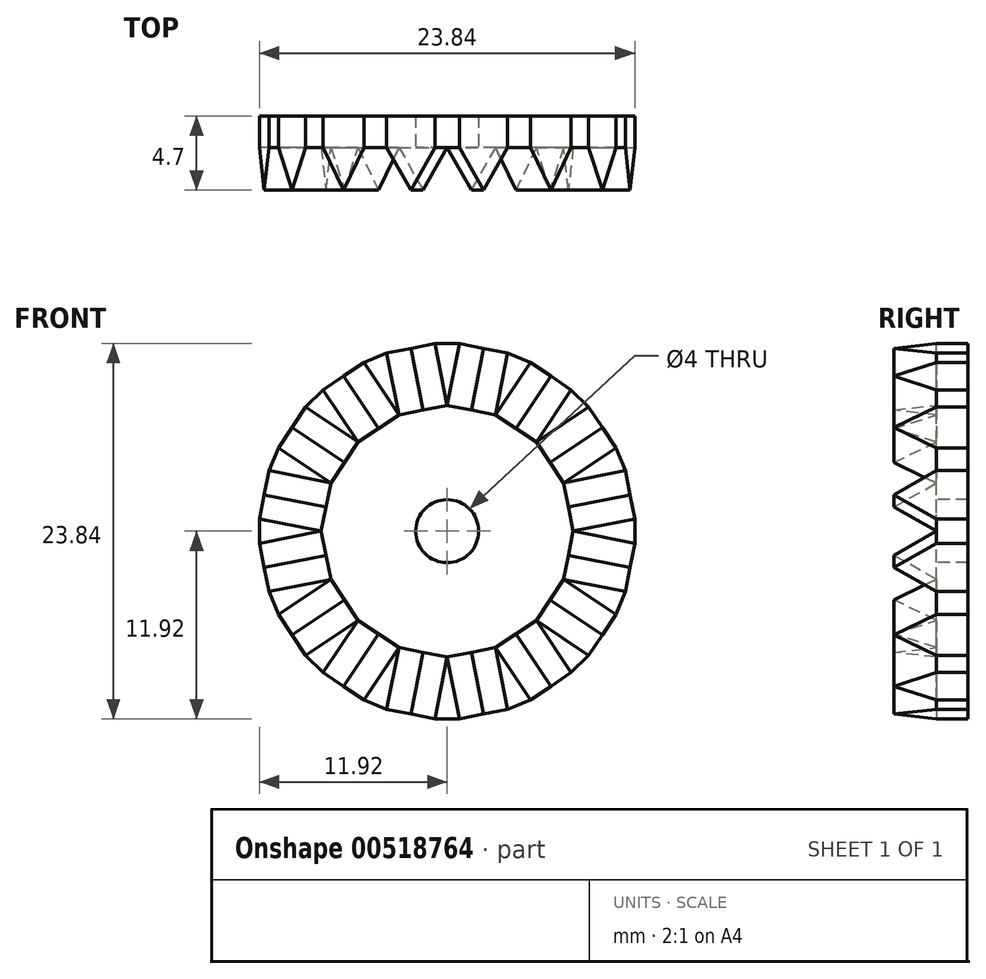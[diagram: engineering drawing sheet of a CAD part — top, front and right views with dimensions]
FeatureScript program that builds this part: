
annotation { "Feature Type Name" : "Feature", "Feature Type Description" : "" }
export const myFeature = defineFeature(function(context is Context, id is Id, definition is map)
    precondition{}
    {
        {
            var Q0;
            Q0=qCreatedBy(makeId("Front.planeOp"),FACE);
            var sketch = newSketch(context, id + "F0", { "sketchPlane" : qUnion([Q0])});
            skCircle(sketch, "E0", {"center": v(0, 0) * mm, "radius": 8 * mm, "construction": true});
            skCircle(sketch, "E1", {"center": v(0, 0) * mm, "radius": 2 * mm});
            skLineSegment(sketch, "E2", {"start": v(0, 0) * mm, "end": v(-3.06, 7.4) * mm, "construction": true});
            skLineSegment(sketch, "E3", {"start": v(-3.06, 7.4) * mm, "end": v(0, 8) * mm});
            skLineSegment(sketch, "E4.1.0", {"start": v(-5.66, 5.66) * mm, "end": v(-3.06, 7.4) * mm});
            skLineSegment(sketch, "E4.2.0", {"start": v(-7.4, 3.06) * mm, "end": v(-5.66, 5.66) * mm});
            skLineSegment(sketch, "E4.3.0", {"start": v(-8, 0) * mm, "end": v(-7.4, 3.06) * mm});
            skLineSegment(sketch, "E4.4.0", {"start": v(-7.4, -3.06) * mm, "end": v(-8, 0) * mm});
            skLineSegment(sketch, "E4.5.0", {"start": v(-5.66, -5.66) * mm, "end": v(-7.4, -3.06) * mm});
            skLineSegment(sketch, "E4.6.0", {"start": v(-3.06, -7.4) * mm, "end": v(-5.66, -5.66) * mm});
            skLineSegment(sketch, "E4.7.0", {"start": v(0, -8) * mm, "end": v(-3.06, -7.4) * mm});
            skLineSegment(sketch, "E4.8.0", {"start": v(3.06, -7.4) * mm, "end": v(0, -8) * mm});
            skLineSegment(sketch, "E4.9.0", {"start": v(5.66, -5.66) * mm, "end": v(3.06, -7.4) * mm});
            skLineSegment(sketch, "E4.10.0", {"start": v(7.4, -3.06) * mm, "end": v(5.66, -5.66) * mm});
            skLineSegment(sketch, "E4.11.0", {"start": v(8, 0) * mm, "end": v(7.4, -3.06) * mm});
            skLineSegment(sketch, "E4.12.0", {"start": v(7.4, 3.06) * mm, "end": v(8, 0) * mm});
            skLineSegment(sketch, "E4.13.0", {"start": v(5.66, 5.66) * mm, "end": v(7.4, 3.06) * mm});
            skLineSegment(sketch, "E4.14.0", {"start": v(3.06, 7.4) * mm, "end": v(5.66, 5.66) * mm});
            skLineSegment(sketch, "E4.15.0", {"start": v(0, 8) * mm, "end": v(3.06, 7.4) * mm});
            skLineSegment(sketch, "E5", {"start": v(-3.06, 7.4) * mm, "end": v(-5.28, 10.72) * mm});
            skLineSegment(sketch, "E6", {"start": v(-5.28, 10.72) * mm, "end": v(-3.84, 11.31) * mm});
            skLineSegment(sketch, "E7", {"start": v(-3.84, 11.31) * mm, "end": v(-3.06, 7.4) * mm});
            skLineSegment(sketch, "E8.1.0", {"start": v(-8.98, 7.88) * mm, "end": v(-7.88, 8.98) * mm});
            skLineSegment(sketch, "E8.1.1", {"start": v(-5.66, 5.66) * mm, "end": v(-8.98, 7.88) * mm});
            skLineSegment(sketch, "E8.1.2", {"start": v(-7.88, 8.98) * mm, "end": v(-5.66, 5.66) * mm});
            skLineSegment(sketch, "E8.2.0", {"start": v(-11.31, 3.84) * mm, "end": v(-10.72, 5.28) * mm});
            skLineSegment(sketch, "E8.2.1", {"start": v(-7.4, 3.06) * mm, "end": v(-11.31, 3.84) * mm});
            skLineSegment(sketch, "E8.2.2", {"start": v(-10.72, 5.28) * mm, "end": v(-7.4, 3.06) * mm});
            skLineSegment(sketch, "E8.3.0", {"start": v(-11.92, -0.78) * mm, "end": v(-11.92, 0.78) * mm});
            skLineSegment(sketch, "E8.3.1", {"start": v(-8, 0) * mm, "end": v(-11.92, -0.78) * mm});
            skLineSegment(sketch, "E8.3.2", {"start": v(-11.92, 0.78) * mm, "end": v(-8, 0) * mm});
            skLineSegment(sketch, "E8.4.0", {"start": v(-10.72, -5.28) * mm, "end": v(-11.31, -3.84) * mm});
            skLineSegment(sketch, "E8.4.1", {"start": v(-7.4, -3.06) * mm, "end": v(-10.72, -5.28) * mm});
            skLineSegment(sketch, "E8.4.2", {"start": v(-11.31, -3.84) * mm, "end": v(-7.4, -3.06) * mm});
            skLineSegment(sketch, "E8.5.0", {"start": v(-7.88, -8.98) * mm, "end": v(-8.98, -7.88) * mm});
            skLineSegment(sketch, "E8.5.1", {"start": v(-5.66, -5.66) * mm, "end": v(-7.88, -8.98) * mm});
            skLineSegment(sketch, "E8.5.2", {"start": v(-8.98, -7.88) * mm, "end": v(-5.66, -5.66) * mm});
            skLineSegment(sketch, "E8.6.0", {"start": v(-3.84, -11.31) * mm, "end": v(-5.28, -10.72) * mm});
            skLineSegment(sketch, "E8.6.1", {"start": v(-3.06, -7.4) * mm, "end": v(-3.84, -11.31) * mm});
            skLineSegment(sketch, "E8.6.2", {"start": v(-5.28, -10.72) * mm, "end": v(-3.06, -7.4) * mm});
            skLineSegment(sketch, "E8.7.0", {"start": v(0.78, -11.92) * mm, "end": v(-0.78, -11.92) * mm});
            skLineSegment(sketch, "E8.7.1", {"start": v(0, -8) * mm, "end": v(0.78, -11.92) * mm});
            skLineSegment(sketch, "E8.7.2", {"start": v(-0.78, -11.92) * mm, "end": v(0, -8) * mm});
            skLineSegment(sketch, "E8.8.0", {"start": v(5.28, -10.72) * mm, "end": v(3.84, -11.31) * mm});
            skLineSegment(sketch, "E8.8.1", {"start": v(3.06, -7.4) * mm, "end": v(5.28, -10.72) * mm});
            skLineSegment(sketch, "E8.8.2", {"start": v(3.84, -11.31) * mm, "end": v(3.06, -7.4) * mm});
            skLineSegment(sketch, "E8.9.0", {"start": v(8.98, -7.88) * mm, "end": v(7.88, -8.98) * mm});
            skLineSegment(sketch, "E8.9.1", {"start": v(5.66, -5.66) * mm, "end": v(8.98, -7.88) * mm});
            skLineSegment(sketch, "E8.9.2", {"start": v(7.88, -8.98) * mm, "end": v(5.66, -5.66) * mm});
            skLineSegment(sketch, "E8.10.0", {"start": v(11.31, -3.84) * mm, "end": v(10.72, -5.28) * mm});
            skLineSegment(sketch, "E8.10.1", {"start": v(7.4, -3.06) * mm, "end": v(11.31, -3.84) * mm});
            skLineSegment(sketch, "E8.10.2", {"start": v(10.72, -5.28) * mm, "end": v(7.4, -3.06) * mm});
            skLineSegment(sketch, "E8.11.0", {"start": v(11.92, 0.78) * mm, "end": v(11.92, -0.78) * mm});
            skLineSegment(sketch, "E8.11.1", {"start": v(8, 0) * mm, "end": v(11.92, 0.78) * mm});
            skLineSegment(sketch, "E8.11.2", {"start": v(11.92, -0.78) * mm, "end": v(8, 0) * mm});
            skLineSegment(sketch, "E8.12.0", {"start": v(10.72, 5.28) * mm, "end": v(11.31, 3.84) * mm});
            skLineSegment(sketch, "E8.12.1", {"start": v(7.4, 3.06) * mm, "end": v(10.72, 5.28) * mm});
            skLineSegment(sketch, "E8.12.2", {"start": v(11.31, 3.84) * mm, "end": v(7.4, 3.06) * mm});
            skLineSegment(sketch, "E8.13.0", {"start": v(7.88, 8.98) * mm, "end": v(8.98, 7.88) * mm});
            skLineSegment(sketch, "E8.13.1", {"start": v(5.66, 5.66) * mm, "end": v(7.88, 8.98) * mm});
            skLineSegment(sketch, "E8.13.2", {"start": v(8.98, 7.88) * mm, "end": v(5.66, 5.66) * mm});
            skLineSegment(sketch, "E8.14.0", {"start": v(3.84, 11.31) * mm, "end": v(5.28, 10.72) * mm});
            skLineSegment(sketch, "E8.14.1", {"start": v(3.06, 7.4) * mm, "end": v(3.84, 11.31) * mm});
            skLineSegment(sketch, "E8.14.2", {"start": v(5.28, 10.72) * mm, "end": v(3.06, 7.4) * mm});
            skLineSegment(sketch, "E8.15.0", {"start": v(-0.78, 11.92) * mm, "end": v(0.78, 11.92) * mm});
            skLineSegment(sketch, "E8.15.1", {"start": v(0, 8) * mm, "end": v(-0.78, 11.92) * mm});
            skLineSegment(sketch, "E8.15.2", {"start": v(0.78, 11.92) * mm, "end": v(0, 8) * mm});
            skSolve(sketch);
        }
        {
            var Q0;
            Q0 = qSketchRegion(id + "F0", true);
            extrude(context, id + "F1", {"entities" : qUnion([Q0]), "oppositeDirection" : true, "depth" : 2 * mm, "offsetDistance" : 25 * mm});
        }
        {
            var Q0;
            Q0=makeQuery(id+"F1.opExtrude","SWEPT_FACE",FACE,{"disambiguationData":[OSD([sQuery(id+"F0.wireOp",EDGE,"E3")])]});
            var sketch = newSketch(context, id + "F2", { "sketchPlane" : qUnion([Q0])});
            skLineSegment(sketch, "E9", {"start": v(-1.56, 0) * mm, "end": v(0, -2.7) * mm});
            skLineSegment(sketch, "E10", {"start": v(0, -2.7) * mm, "end": v(1.56, 0) * mm});
            skLineSegment(sketch, "E11", {"start": v(-1.56, 0) * mm, "end": v(-1.56, 2) * mm});
            skLineSegment(sketch, "E12", {"start": v(-1.56, 2) * mm, "end": v(1.56, 2) * mm});
            skLineSegment(sketch, "E13", {"start": v(1.56, 2) * mm, "end": v(1.56, 0) * mm});
            skSolve(sketch);
        }
        {
            var Q0;
            Q0 = qSketchRegion(id + "F2", true);
            extrude(context, id + "F3", {"entities" : qUnion([Q0]), "operationType" : NewBodyOperationType.ADD, "depth" : 4 * mm, "offsetDistance" : 25 * mm});
        }
        {
            var Q0;
            Q0=makeQuery(id+"F1.opExtrude","SWEPT_BODY",BODY,{"disambiguationData":[OSD([sQuery(id+"F0.wireOp",EDGE,"E1"),sQuery(id+"F0.wireOp",EDGE,"E3"),sQuery(id+"F0.wireOp",EDGE,"E4.1.0"),sQuery(id+"F0.wireOp",EDGE,"E4.2.0"),sQuery(id+"F0.wireOp",EDGE,"E4.3.0"),sQuery(id+"F0.wireOp",EDGE,"E4.4.0"),sQuery(id+"F0.wireOp",EDGE,"E4.5.0"),sQuery(id+"F0.wireOp",EDGE,"E4.6.0"),sQuery(id+"F0.wireOp",EDGE,"E4.7.0"),sQuery(id+"F0.wireOp",EDGE,"E4.8.0"),sQuery(id+"F0.wireOp",EDGE,"E4.9.0"),sQuery(id+"F0.wireOp",EDGE,"E4.10.0"),sQuery(id+"F0.wireOp",EDGE,"E4.11.0"),sQuery(id+"F0.wireOp",EDGE,"E4.12.0"),sQuery(id+"F0.wireOp",EDGE,"E4.13.0"),sQuery(id+"F0.wireOp",EDGE,"E4.14.0"),sQuery(id+"F0.wireOp",EDGE,"E4.15.0")])]});
            var Q1;
            Q1=makeQuery(id+"F1.opExtrude","CAP_EDGE",EDGE,{"disambiguationData":[OSD([sQuery(id+"F0.wireOp",EDGE,"E1")])],"isStart":true});
            circularPattern(context, id + "F4", {"operationType" : NewBodyOperationType.ADD, "entities" : qUnion([Q0]), "axis" : qUnion([Q1]), "angle" : 360 * degree, "instanceCount" : 16, "equalSpace" : true});
        }
    });
